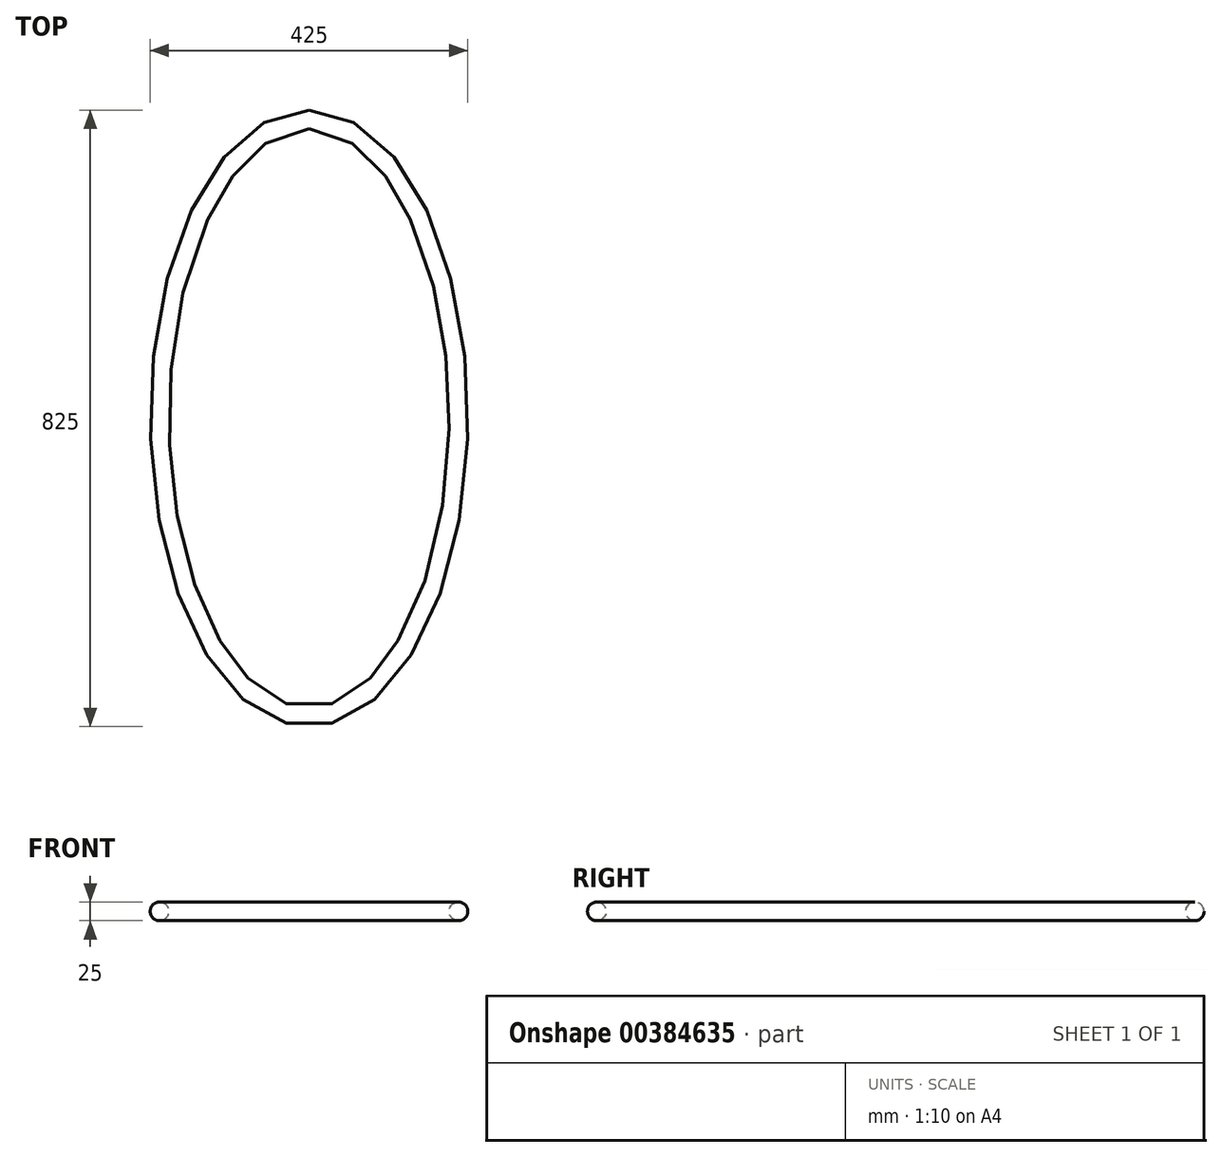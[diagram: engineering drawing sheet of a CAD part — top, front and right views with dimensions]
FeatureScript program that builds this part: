
annotation { "Feature Type Name" : "Feature", "Feature Type Description" : "" }
export const myFeature = defineFeature(function(context is Context, id is Id, definition is map)
    precondition{}
    {
        {
            var Q0;
            Q0=qCreatedBy(makeId("Top.planeOp"),FACE);
            var sketch = newSketch(context, id + "F0", { "sketchPlane" : qUnion([Q0])});
            skLineSegment(sketch, "E0", {"start": v(0, 0) * mm, "end": v(0, 400) * mm});
            skLineSegment(sketch, "E1", {"start": v(0, 400) * mm, "end": v(200, 400) * mm});
            skLineSegment(sketch, "E2", {"start": v(200, 400) * mm, "end": v(200, -400) * mm});
            skLineSegment(sketch, "E3", {"start": v(200, -400) * mm, "end": v(-200, -400) * mm});
            skLineSegment(sketch, "E4", {"start": v(-200, -400) * mm, "end": v(-200, 400) * mm});
            skLineSegment(sketch, "E5", {"start": v(-200, 400) * mm, "end": v(0, 400) * mm});
            skEllipse(sketch, "E6", {"center": v(0, 0) * mm, "majorRadius": 200 * mm, "minorRadius": 400 * mm, "majorAxis": v(-1, 0)});
            skLineSegment(sketch, "E7", {"start": v(0, 0) * mm, "end": v(-200, 0) * mm});
            skLineSegment(sketch, "E8", {"start": v(0, 0) * mm, "end": v(0, -400) * mm});
            skSolve(sketch);
        }
        {
            var Q0;
            Q0=qCreatedBy(makeId("Right.planeOp"),FACE);
            var sketch = newSketch(context, id + "F1", { "sketchPlane" : qUnion([Q0])});
            skCircle(sketch, "E9", {"center": v(400, 0) * mm, "radius": 12.5 * mm});
            skSolve(sketch);
        }
        {
            var Q0;
            Q0=makeQuery(id+"F1.imprint","IMPRINT",FACE,{"disambiguationData":[TD([[makeQuery(id+"F1.imprint","IMPRINT",EDGE,{"derivedFrom":sQuery(id+"F1.wireOp",EDGE,"E9")}),1.0]])]});
            var Q1;
            Q1=sQuery(id+"F1.wireOp",EDGE,"E9");
            var Q2;
            Q2=sQuery(id+"F0.wireOp",EDGE,"E6");
            sweep(context, id + "F2", {"bodyType" : ToolBodyType.SURFACE, "profiles" : qUnion([Q0]), "surfaceProfiles" : qUnion([Q1]), "path" : qUnion([Q2])});
        }
    });
